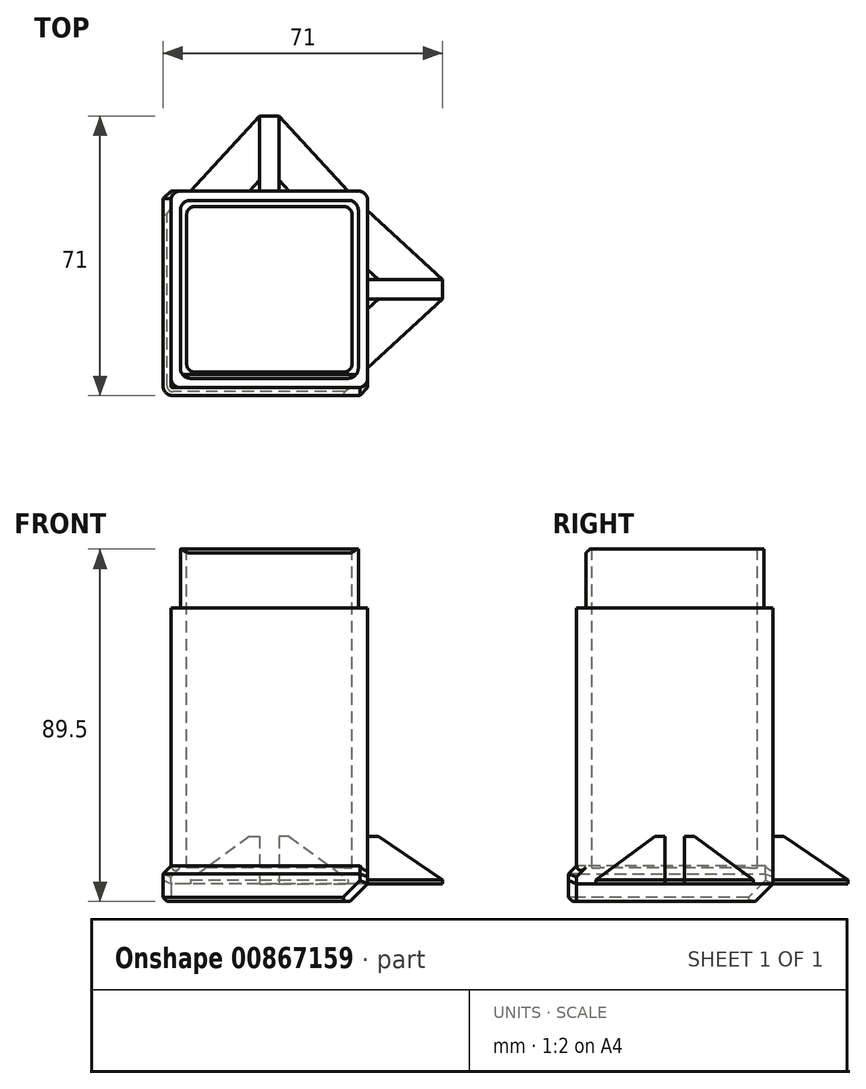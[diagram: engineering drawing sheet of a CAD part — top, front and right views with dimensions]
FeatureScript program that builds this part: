
annotation { "Feature Type Name" : "Feature", "Feature Type Description" : "" }
export const myFeature = defineFeature(function(context is Context, id is Id, definition is map)
    precondition{}
    {
        {
            var Q0;
            Q0=qCreatedBy(makeId("Top.planeOp"),FACE);
            var sketch = newSketch(context, id + "F0", { "sketchPlane" : qUnion([Q0])});
            skLineSegment(sketch, "E0.bottom", {"start": v(25, 25) * mm, "end": v(-25, 25) * mm});
            skLineSegment(sketch, "E0.top", {"start": v(25, -25) * mm, "end": v(-25, -25) * mm});
            skLineSegment(sketch, "E0.left", {"start": v(25, 25) * mm, "end": v(25, -25) * mm});
            skLineSegment(sketch, "E0.right", {"start": v(-25, 25) * mm, "end": v(-25, -25) * mm});
            skPoint(sketch, "E0.middle", {"position": v(0, 0) * mm});
            skSolve(sketch);
        }
        {
            var Q0;
            Q0 = qSketchRegion(id + "F0", true);
            extrude(context, id + "F1", {"entities" : qUnion([Q0]), "depth" : 70 * mm, "offsetDistance" : 25 * mm});
        }
        {
            var Q0;
            Q0=makeQuery(id+"F1.opExtrude","CAP_FACE",FACE,{"disambiguationData":[OSD([sQuery(id+"F0.wireOp",EDGE,"E0.bottom"),sQuery(id+"F0.wireOp",EDGE,"E0.top"),sQuery(id+"F0.wireOp",EDGE,"E0.left"),sQuery(id+"F0.wireOp",EDGE,"E0.right")])],"isStart":false});
            var sketch = newSketch(context, id + "F2", { "sketchPlane" : qUnion([Q0])});
            skLineSegment(sketch, "E1.bottom", {"start": v(22.6, 22.6) * mm, "end": v(-22.6, 22.6) * mm});
            skLineSegment(sketch, "E1.top", {"start": v(22.6, -22.6) * mm, "end": v(-22.6, -22.6) * mm});
            skLineSegment(sketch, "E1.left", {"start": v(22.6, 22.6) * mm, "end": v(22.6, -22.6) * mm});
            skLineSegment(sketch, "E1.right", {"start": v(-22.6, 22.6) * mm, "end": v(-22.6, -22.6) * mm});
            skPoint(sketch, "E1.middle", {"position": v(0, 0) * mm});
            skSolve(sketch);
        }
        {
            var Q0;
            Q0 = qSketchRegion(id + "F2", true);
            extrude(context, id + "F3", {"entities" : qUnion([Q0]), "operationType" : NewBodyOperationType.ADD, "depth" : 15 * mm, "offsetDistance" : 25 * mm});
        }
        {
            var Q0;
            Q0=makeQuery(id+"F2.imprint","IMPRINT",FACE,{"disambiguationData":[TD([[makeQuery(id+"F2.imprint","IMPRINT",EDGE,{"derivedFrom":sQuery(id+"F2.wireOp",EDGE,"E1.bottom")}),-1.0]])]});
            var sketch = newSketch(context, id + "F4", { "sketchPlane" : qUnion([Q0])});
            skLineSegment(sketch, "E2.bottom", {"start": v(21, 21) * mm, "end": v(-21, 21) * mm});
            skLineSegment(sketch, "E2.top", {"start": v(21, -21) * mm, "end": v(-21, -21) * mm});
            skLineSegment(sketch, "E2.left", {"start": v(21, 21) * mm, "end": v(21, -21) * mm});
            skLineSegment(sketch, "E2.right", {"start": v(-21, 21) * mm, "end": v(-21, -21) * mm});
            skPoint(sketch, "E2.middle", {"position": v(0, 0) * mm});
            skSolve(sketch);
        }
        {
            var Q0;
            Q0 = qSketchRegion(id + "F4", true);
            extrude(context, id + "F5", {"entities" : qUnion([Q0]), "operationType" : NewBodyOperationType.REMOVE, "oppositeDirection" : true, "depth" : 66 * mm, "offsetDistance" : 25 * mm, "hasSecondDirection" : true, "secondDirectionBound" : SecondDirectionBoundingType.UP_TO_NEXT, "secondDirectionOppositeDirection" : false, "secondDirectionDepth" : 25 * mm});
        }
        {
            var Q0;
            Q0=makeQuery(id+"F5.boolean.opBoolean","COPY",EDGE,{"derivedFrom":makeQuery(id+"F5.opExtrude","SWEPT_EDGE",EDGE,{"disambiguationData":[OSD([sQuery(id+"F4.wireOp",EDGE,"E2.top"),sQuery(id+"F4.wireOp",EDGE,"E2.right")])]})});
            var Q1;
            Q1=makeQuery(id+"F5.boolean.opBoolean","COPY",EDGE,{"derivedFrom":makeQuery(id+"F5.opExtrude","SWEPT_EDGE",EDGE,{"disambiguationData":[OSD([sQuery(id+"F4.wireOp",EDGE,"E2.bottom"),sQuery(id+"F4.wireOp",EDGE,"E2.right")])]})});
            var Q2;
            Q2=makeQuery(id+"F5.boolean.opBoolean","COPY",EDGE,{"derivedFrom":makeQuery(id+"F5.opExtrude","SWEPT_EDGE",EDGE,{"disambiguationData":[OSD([sQuery(id+"F4.wireOp",EDGE,"E2.bottom"),sQuery(id+"F4.wireOp",EDGE,"E2.left")])]})});
            var Q3;
            Q3=makeQuery(id+"F5.boolean.opBoolean","COPY",EDGE,{"derivedFrom":makeQuery(id+"F5.opExtrude","SWEPT_EDGE",EDGE,{"disambiguationData":[OSD([sQuery(id+"F4.wireOp",EDGE,"E2.top"),sQuery(id+"F4.wireOp",EDGE,"E2.left")])]})});
            fillet(context, id + "F6", {"entities" : qUnion([Q0, Q1, Q2, Q3]), "radius" : 2 * mm, "tangentPropagation" : true, "allowEdgeOverflow" : false});
        }
        {
            var Q0;
            Q0=makeQuery(id+"F3.opExtrude","CAP_EDGE",EDGE,{"disambiguationData":[OSD([sQuery(id+"F2.wireOp",EDGE,"E1.top")])],"isStart":false});
            chamfer(context, id + "F7", {"entities" : qUnion([Q0]), "width" : 1 * mm, "tangentPropagation" : true});
        }
        {
            var Q0;
            Q0=qCreatedBy(makeId("Top.planeOp"),FACE);
            var sketch = newSketch(context, id + "F8", { "sketchPlane" : qUnion([Q0])});
            skLineSegment(sketch, "E3", {"start": v(25, 20) * mm, "end": v(25, -20) * mm});
            skPoint(sketch, "E4", {"position": v(25, 0) * mm});
            skLineSegment(sketch, "E5", {"start": v(44, 2.5) * mm, "end": v(25, 20) * mm});
            skLineSegment(sketch, "E6", {"start": v(44, -2.5) * mm, "end": v(25, -20) * mm});
            skPoint(sketch, "E7", {"position": v(44, 2.5) * mm});
            skPoint(sketch, "E8", {"position": v(44, -2.5) * mm});
            skLineSegment(sketch, "E9", {"start": v(44, 2.5) * mm, "end": v(44, -2.5) * mm});
            skSolve(sketch);
        }
        {
            var Q0;
            Q0 = qSketchRegion(id + "F8", true);
            extrude(context, id + "F9", {"entities" : qUnion([Q0]), "operationType" : NewBodyOperationType.ADD, "depth" : 12 * mm, "offsetDistance" : 25 * mm});
        }
        {
            var Q0;
            Q0=makeQuery(id+"F9.opExtrude","CAP_EDGE",EDGE,{"disambiguationData":[OSD([sQuery(id+"F8.wireOp",EDGE,"E5")])],"isStart":false});
            var Q1;
            Q1=makeQuery(id+"F9.opExtrude","CAP_EDGE",EDGE,{"disambiguationData":[OSD([sQuery(id+"F8.wireOp",EDGE,"E6")])],"isStart":false});
            chamfer(context, id + "F10", {"entities" : qUnion([Q0, Q1]), "width" : 11 * mm, "tangentPropagation" : true});
        }
        {
            var Q0;
            Q0=qCreatedBy(makeId("Top.planeOp"),FACE);
            cPlane(context, id + "F11", {"entities" : qUnion([Q0]), "cplaneType" : CPlaneType.OFFSET, "offset" : 1 * mm, "width" : 150 * mm, "height" : 150 * mm});
        }
        {
            var Q0;
            Q0=qCreatedBy(id+"F11.planeOp",FACE);
            var sketch = newSketch(context, id + "F12", { "sketchPlane" : qUnion([Q0])});
            skLineSegment(sketch, "E10.bottom", {"start": v(25, 2.5) * mm, "end": v(45, 2.5) * mm});
            skLineSegment(sketch, "E10.top", {"start": v(25, -2.5) * mm, "end": v(45, -2.5) * mm});
            skLineSegment(sketch, "E10.left", {"start": v(25, 2.5) * mm, "end": v(25, -2.5) * mm});
            skLineSegment(sketch, "E10.right", {"start": v(45, 2.5) * mm, "end": v(45, -2.5) * mm});
            skPoint(sketch, "E11", {"position": v(25, 0) * mm});
            skSolve(sketch);
        }
        {
            var Q0;
            Q0 = qSketchRegion(id + "F12", true);
            extrude(context, id + "F13", {"entities" : qUnion([Q0]), "operationType" : NewBodyOperationType.REMOVE, "depth" : 20 * mm, "offsetDistance" : 25 * mm});
        }
        {
            var Q0;
            Q0=qCreatedBy(makeId("Top.planeOp"),FACE);
            var sketch = newSketch(context, id + "F14", { "sketchPlane" : qUnion([Q0])});
            skLineSegment(sketch, "E12", {"start": v(-20, 25) * mm, "end": v(20, 25) * mm});
            skLineSegment(sketch, "E13", {"start": v(-2.5, 44) * mm, "end": v(-20, 25) * mm});
            skLineSegment(sketch, "E14", {"start": v(2.5, 44) * mm, "end": v(20, 25) * mm});
            skLineSegment(sketch, "E15", {"start": v(-2.5, 44) * mm, "end": v(2.5, 44) * mm});
            skPoint(sketch, "E16", {"position": v(0, 44) * mm});
            skSolve(sketch);
        }
        {
            var Q0;
            Q0 = qSketchRegion(id + "F14", true);
            extrude(context, id + "F15", {"entities" : qUnion([Q0]), "operationType" : NewBodyOperationType.ADD, "depth" : 12 * mm, "offsetDistance" : 25 * mm});
        }
        {
            var Q0;
            Q0=makeQuery(id+"F15.opExtrude","CAP_EDGE",EDGE,{"disambiguationData":[OSD([sQuery(id+"F14.wireOp",EDGE,"E13")])],"isStart":false});
            var Q1;
            Q1=makeQuery(id+"F15.opExtrude","CAP_EDGE",EDGE,{"disambiguationData":[OSD([sQuery(id+"F14.wireOp",EDGE,"E14")])],"isStart":false});
            chamfer(context, id + "F16", {"entities" : qUnion([Q0, Q1]), "width" : 11 * mm, "tangentPropagation" : true});
        }
        {
            var Q0;
            Q0=qCreatedBy(id+"F11.planeOp",FACE);
            var sketch = newSketch(context, id + "F17", { "sketchPlane" : qUnion([Q0])});
            skLineSegment(sketch, "E17.bottom", {"start": v(-2.5, 25) * mm, "end": v(-2.5, 45) * mm});
            skLineSegment(sketch, "E17.top", {"start": v(2.5, 25) * mm, "end": v(2.5, 45) * mm});
            skLineSegment(sketch, "E17.left", {"start": v(-2.5, 25) * mm, "end": v(2.5, 25) * mm});
            skLineSegment(sketch, "E17.right", {"start": v(-2.5, 45) * mm, "end": v(2.5, 45) * mm});
            skPoint(sketch, "E18", {"position": v(0, 25) * mm});
            skSolve(sketch);
        }
        {
            var Q0;
            Q0 = qSketchRegion(id + "F17", true);
            extrude(context, id + "F18", {"entities" : qUnion([Q0]), "operationType" : NewBodyOperationType.REMOVE, "depth" : 20 * mm, "offsetDistance" : 25 * mm});
        }
        {
            var Q0;
            Q0=qCreatedBy(makeId("Top.planeOp"),FACE);
            var sketch = newSketch(context, id + "F19", { "sketchPlane" : qUnion([Q0])});
            skLineSegment(sketch, "E19.top", {"start": v(-27, -27) * mm, "end": v(25, -27) * mm});
            skLineSegment(sketch, "E19.left", {"start": v(-27, 25) * mm, "end": v(-27, -27) * mm});
            skPoint(sketch, "E20", {"position": v(-25, 25) * mm});
            skPoint(sketch, "E21", {"position": v(25, -25) * mm});
            skLineSegment(sketch, "E22", {"start": v(-25, 25) * mm, "end": v(-25, -25) * mm});
            skLineSegment(sketch, "E23", {"start": v(-25, -25) * mm, "end": v(25, -25) * mm});
            skLineSegment(sketch, "E24", {"start": v(-27, 25) * mm, "end": v(-25, 25) * mm});
            skLineSegment(sketch, "E25", {"start": v(25, -27) * mm, "end": v(25, -25) * mm});
            skSolve(sketch);
        }
        {
            var Q0;
            Q0 = qSketchRegion(id + "F19", true);
            extrude(context, id + "F20", {"entities" : qUnion([Q0]), "operationType" : NewBodyOperationType.ADD, "endBound" : BoundingType.SYMMETRIC, "oppositeDirection" : true, "depth" : 9 * mm, "offsetDistance" : 25 * mm, "hasSecondDirection" : true, "secondDirectionOppositeDirection" : false, "secondDirectionDepth" : 25 * mm});
        }
        {
            var Q0;
            Q0=makeQuery(id+"F1.opExtrude","SWEPT_EDGE",EDGE,{"disambiguationData":[OSD([sQuery(id+"F0.wireOp",EDGE,"E0.bottom"),sQuery(id+"F0.wireOp",EDGE,"E0.left")])]});
            var Q1;
            Q1=makeQuery(id+"F3.opExtrude","SWEPT_EDGE",EDGE,{"disambiguationData":[OSD([sQuery(id+"F2.wireOp",EDGE,"E1.bottom"),sQuery(id+"F2.wireOp",EDGE,"E1.right")])]});
            var Q2;
            Q2=makeQuery(id+"F1.opExtrude","SWEPT_EDGE",EDGE,{"disambiguationData":[OSD([sQuery(id+"F0.wireOp",EDGE,"E0.bottom"),sQuery(id+"F0.wireOp",EDGE,"E0.right")])]});
            var Q3;
            Q3=makeQuery(id+"F3.opExtrude","SWEPT_EDGE",EDGE,{"disambiguationData":[OSD([sQuery(id+"F2.wireOp",EDGE,"E1.bottom"),sQuery(id+"F2.wireOp",EDGE,"E1.left")])]});
            var Q4;
            Q4=makeQuery(id+"F3.opExtrude","SWEPT_EDGE",EDGE,{"disambiguationData":[OSD([sQuery(id+"F2.wireOp",EDGE,"E1.top"),sQuery(id+"F2.wireOp",EDGE,"E1.left")])]});
            var Q5;
            Q5=makeQuery(id+"F1.opExtrude","SWEPT_EDGE",EDGE,{"disambiguationData":[OSD([sQuery(id+"F0.wireOp",EDGE,"E0.top"),sQuery(id+"F0.wireOp",EDGE,"E0.left")])]});
            var Q6;
            Q6=makeQuery(id+"F3.opExtrude","SWEPT_EDGE",EDGE,{"disambiguationData":[OSD([sQuery(id+"F2.wireOp",EDGE,"E1.top"),sQuery(id+"F2.wireOp",EDGE,"E1.right")])]});
            var Q7;
            Q7=makeQuery(id+"F1.opExtrude","SWEPT_EDGE",EDGE,{"disambiguationData":[OSD([sQuery(id+"F0.wireOp",EDGE,"E0.top"),sQuery(id+"F0.wireOp",EDGE,"E0.right")])]});
            var Q8;
            Q8=makeQuery(id+"F20.opExtrude","SWEPT_EDGE",EDGE,{"disambiguationData":[OSD([sQuery(id+"F19.wireOp",EDGE,"E19.top"),sQuery(id+"F19.wireOp",EDGE,"E19.left")])]});
            fillet(context, id + "F21", {"entities" : qUnion([Q0, Q1, Q2, Q3, Q4, Q5, Q6, Q7, Q8]), "radius" : 2.5 * mm, "tangentPropagation" : true, "allowEdgeOverflow" : false});
        }
        {
            var Q0;
            Q0=makeQuery(id+"F20.opExtrude","CAP_EDGE",EDGE,{"disambiguationData":[OSD([sQuery(id+"F19.wireOp",EDGE,"E19.left")])],"isStart":true});
            chamfer(context, id + "F22", {"entities" : qUnion([Q0]), "width" : 2 * mm, "tangentPropagation" : true});
        }
        {
            var Q0;
            Q0=makeQuery(id+"F20.opExtrude","CAP_EDGE",EDGE,{"disambiguationData":[OSD([sQuery(id+"F19.wireOp",EDGE,"E24")])],"isStart":false});
            var Q1;
            Q1=makeQuery(id+"F20.opExtrude","CAP_EDGE",EDGE,{"disambiguationData":[OSD([sQuery(id+"F19.wireOp",EDGE,"E25")])],"isStart":false});
            chamfer(context, id + "F23", {"entities" : qUnion([Q0, Q1]), "width" : 4.5 * mm, "tangentPropagation" : true});
        }
        {
            var Q0;
            Q0=makeQuery(id+"F22.opChamfer","BLEND_EDGE",EDGE,{"blendedFrom":[makeQuery(id+"F20.opExtrude","CAP_EDGE",EDGE,{"disambiguationData":[OSD([sQuery(id+"F19.wireOp",EDGE,"E19.left")])],"isStart":true}),makeQuery(id+"F20.opExtrude","SWEPT_FACE",FACE,{"disambiguationData":[OSD([sQuery(id+"F19.wireOp",EDGE,"E24")])]})],"blendedInto":[makeQuery(id+"F20.opExtrude","SWEPT_FACE",FACE,{"disambiguationData":[OSD([sQuery(id+"F19.wireOp",EDGE,"E24")])]})]});
            var Q1;
            Q1=makeQuery(id+"F20.opExtrude","SWEPT_EDGE",EDGE,{"disambiguationData":[OSD([sQuery(id+"F19.wireOp",EDGE,"E19.left"),sQuery(id+"F19.wireOp",EDGE,"E24")])]});
            var Q2;
            Q2=makeQuery(id+"F22.opChamfer","BLEND_EDGE",EDGE,{"blendedFrom":[makeQuery(id+"F20.opExtrude","CAP_EDGE",EDGE,{"disambiguationData":[OSD([sQuery(id+"F19.wireOp",EDGE,"E19.top")])],"isStart":true}),makeQuery(id+"F20.opExtrude","SWEPT_FACE",FACE,{"disambiguationData":[OSD([sQuery(id+"F19.wireOp",EDGE,"E25")])]})],"blendedInto":[makeQuery(id+"F20.opExtrude","SWEPT_FACE",FACE,{"disambiguationData":[OSD([sQuery(id+"F19.wireOp",EDGE,"E25")])]})]});
            var Q3;
            Q3=makeQuery(id+"F20.opExtrude","SWEPT_EDGE",EDGE,{"disambiguationData":[OSD([sQuery(id+"F19.wireOp",EDGE,"E19.top"),sQuery(id+"F19.wireOp",EDGE,"E25")])]});
            var Q4;
            Q4=makeQuery(id+"F23.opChamfer","BLEND_EDGE",EDGE,{"blendedFrom":[makeQuery(id+"F20.opExtrude","CAP_EDGE",EDGE,{"disambiguationData":[OSD([sQuery(id+"F19.wireOp",EDGE,"E24")])],"isStart":false}),makeQuery(id+"F20.opExtrude","SWEPT_FACE",FACE,{"disambiguationData":[OSD([sQuery(id+"F19.wireOp",EDGE,"E19.left")])]})],"blendedInto":[makeQuery(id+"F20.opExtrude","SWEPT_FACE",FACE,{"disambiguationData":[OSD([sQuery(id+"F19.wireOp",EDGE,"E19.left")])]})]});
            var Q5;
            Q5=makeQuery(id+"F23.opChamfer","BLEND_EDGE",EDGE,{"blendedFrom":[makeQuery(id+"F20.opExtrude","CAP_EDGE",EDGE,{"disambiguationData":[OSD([sQuery(id+"F19.wireOp",EDGE,"E25")])],"isStart":false}),makeQuery(id+"F20.opExtrude","SWEPT_FACE",FACE,{"disambiguationData":[OSD([sQuery(id+"F19.wireOp",EDGE,"E19.top")])]})],"blendedInto":[makeQuery(id+"F20.opExtrude","SWEPT_FACE",FACE,{"disambiguationData":[OSD([sQuery(id+"F19.wireOp",EDGE,"E19.top")])]})]});
            chamfer(context, id + "F24", {"entities" : qUnion([Q0, Q1, Q2, Q3, Q4, Q5]), "width" : 2 * mm, "tangentPropagation" : true});
        }
        {
            var Q0;
            Q0=makeQuery(id+"F20.opExtrude","CAP_EDGE",EDGE,{"disambiguationData":[OSD([sQuery(id+"F19.wireOp",EDGE,"E19.left")])],"isStart":false});
            chamfer(context, id + "F25", {"entities" : qUnion([Q0]), "width" : 1 * mm, "tangentPropagation" : true});
        }
    });
